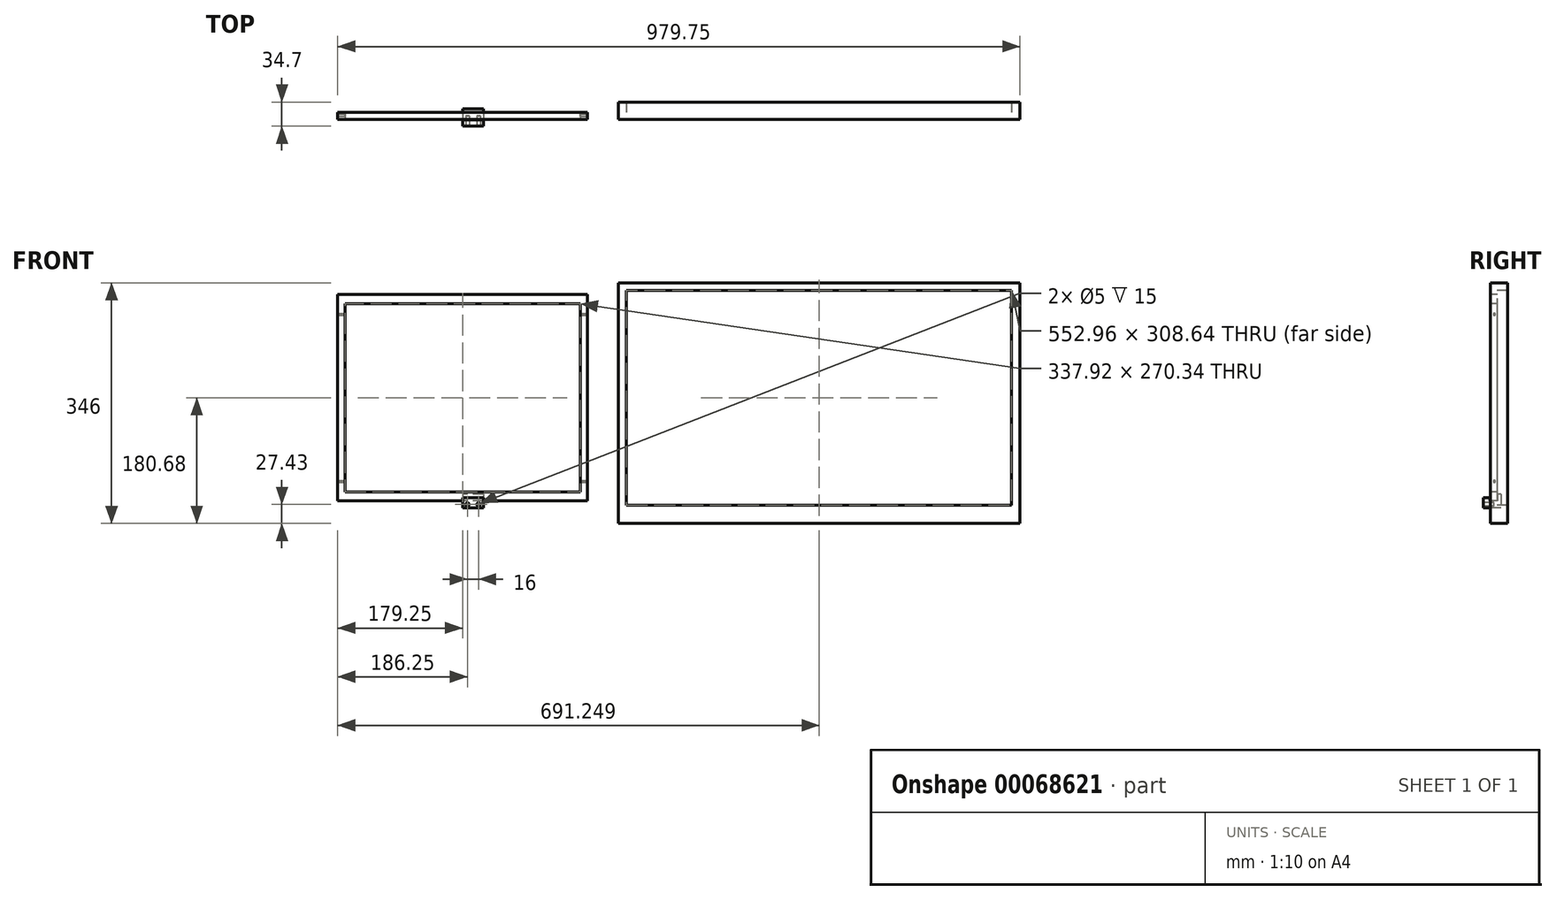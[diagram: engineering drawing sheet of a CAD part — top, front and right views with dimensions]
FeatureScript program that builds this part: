
annotation { "Feature Type Name" : "Feature", "Feature Type Description" : "" }
export const myFeature = defineFeature(function(context is Context, id is Id, definition is map)
    precondition{}
    {
        {
            var Q0;
            Q0=qCreatedBy(makeId("Front.planeOp"),FACE);
            var sketch = newSketch(context, id + "F0", { "sketchPlane" : qUnion([Q0])});
            skLineSegment(sketch, "E0.bottom", {"start": v(168.96, -135.17) * mm, "end": v(-168.96, -135.17) * mm});
            skLineSegment(sketch, "E0.top", {"start": v(168.96, 135.17) * mm, "end": v(-168.96, 135.17) * mm});
            skLineSegment(sketch, "E0.left", {"start": v(168.96, -135.17) * mm, "end": v(168.96, 135.17) * mm});
            skLineSegment(sketch, "E0.right", {"start": v(-168.96, -135.17) * mm, "end": v(-168.96, 135.17) * mm});
            skPoint(sketch, "E0.middle", {"position": v(0, 0) * mm});
            skLineSegment(sketch, "E1.bottom", {"start": v(179.25, -148.25) * mm, "end": v(-179.25, -148.25) * mm});
            skLineSegment(sketch, "E1.top", {"start": v(179.25, 148.25) * mm, "end": v(-179.25, 148.25) * mm});
            skLineSegment(sketch, "E1.left", {"start": v(179.25, -148.25) * mm, "end": v(179.25, 148.25) * mm});
            skLineSegment(sketch, "E1.right", {"start": v(-179.25, -148.25) * mm, "end": v(-179.25, 148.25) * mm});
            skSolve(sketch);
        }
        {
            var Q0;
            Q0 = qSketchRegion(id + "F0", true);
            extrude(context, id + "F1", {"entities" : qUnion([Q0]), "oppositeDirection" : true, "depth" : 10.3 * mm});
        }
        {
            var Q0;
            Q0=makeQuery(id+"F1.opExtrude","SWEPT_FACE",FACE,{"disambiguationData":[OSD([sQuery(id+"F0.wireOp",EDGE,"E1.left")])]});
            var sketch = newSketch(context, id + "F2", { "sketchPlane" : qUnion([Q0])});
            skCircle(sketch, "E2", {"center": v(6, 120) * mm, "radius": 1.5 * mm});
            skCircle(sketch, "E3", {"center": v(6, -120) * mm, "radius": 1.5 * mm});
            skSolve(sketch);
        }
        {
            var Q0;
            Q0 = qSketchRegion(id + "F2", true);
            extrude(context, id + "F3", {"entities" : qUnion([Q0]), "operationType" : NewBodyOperationType.REMOVE, "oppositeDirection" : true, "depth" : 390 * mm});
        }
        {
            var Q0;
            Q0=qCreatedBy(makeId("Right.planeOp"),FACE);
            var sketch = newSketch(context, id + "F4", { "sketchPlane" : qUnion([Q0])});
            skLineSegment(sketch, "E4.bottom", {"start": v(15.3, -158.25) * mm, "end": v(-9.7, -158.25) * mm});
            skLineSegment(sketch, "E4.left", {"start": v(15.3, -138.25) * mm, "end": v(15.3, -158.25) * mm});
            skLineSegment(sketch, "E4.right", {"start": v(-9.7, -143.25) * mm, "end": v(-9.7, -158.25) * mm});
            skLineSegment(sketch, "E5", {"start": v(15.3, -138.25) * mm, "end": v(10.3, -138.25) * mm});
            skLineSegment(sketch, "E6", {"start": v(10.3, -138.25) * mm, "end": v(10.3, -148.25) * mm});
            skLineSegment(sketch, "E7", {"start": v(10.3, -148.25) * mm, "end": v(-0.7, -148.25) * mm});
            skLineSegment(sketch, "E8", {"start": v(-0.7, -148.25) * mm, "end": v(-0.7, -143.25) * mm});
            skLineSegment(sketch, "E9", {"start": v(-0.7, -143.25) * mm, "end": v(-9.7, -143.25) * mm});
            skSolve(sketch);
        }
        {
            var Q0;
            Q0 = qSketchRegion(id + "F4", true);
            extrude(context, id + "F5", {"entities" : qUnion([Q0]), "depth" : 30 * mm});
        }
        {
            var Q0;
            Q0=makeQuery(id+"F5.opExtrude","SWEPT_FACE",FACE,{"disambiguationData":[OSD([sQuery(id+"F4.wireOp",EDGE,"E4.right")])]});
            var sketch = newSketch(context, id + "F6", { "sketchPlane" : qUnion([Q0])});
            skCircle(sketch, "E10", {"center": v(7, -153.25) * mm, "radius": 2.5 * mm});
            skCircle(sketch, "E11", {"center": v(23, -153.25) * mm, "radius": 2.5 * mm});
            skSolve(sketch);
        }
        {
            var Q0;
            Q0=makeQuery(id+"F6.imprint","IMPRINT",FACE,{"disambiguationData":[TD([[makeQuery(id+"F6.imprint","IMPRINT",EDGE,{"derivedFrom":sQuery(id+"F6.wireOp",EDGE,"E10")}),1.0]])]});
            var Q1;
            Q1=makeQuery(id+"F6.imprint","IMPRINT",FACE,{"disambiguationData":[TD([[makeQuery(id+"F6.imprint","IMPRINT",EDGE,{"derivedFrom":sQuery(id+"F6.wireOp",EDGE,"E11")}),1.0]])]});
            extrude(context, id + "F7", {"entities" : qUnion([Q0, Q1]), "operationType" : NewBodyOperationType.REMOVE, "oppositeDirection" : true, "depth" : 15 * mm});
        }
        {
            var Q0;
            Q0=qCreatedBy(makeId("Front.planeOp"),FACE);
            var sketch = newSketch(context, id + "F8", { "sketchPlane" : qUnion([Q0])});
            skLineSegment(sketch, "E12.bottom", {"start": v(788.48, -154.32) * mm, "end": v(235.52, -154.32) * mm});
            skLineSegment(sketch, "E12.top", {"start": v(788.48, 154.32) * mm, "end": v(235.52, 154.32) * mm});
            skLineSegment(sketch, "E12.left", {"start": v(788.48, -154.32) * mm, "end": v(788.48, 154.32) * mm});
            skLineSegment(sketch, "E12.right", {"start": v(235.52, -154.32) * mm, "end": v(235.52, 154.32) * mm});
            skPoint(sketch, "E12.middle", {"position": v(512, 0) * mm});
            skLineSegment(sketch, "E13.bottom", {"start": v(800.5, -180.68) * mm, "end": v(223.5, -180.68) * mm});
            skLineSegment(sketch, "E13.top", {"start": v(800.5, 165.32) * mm, "end": v(223.5, 165.32) * mm});
            skLineSegment(sketch, "E13.left", {"start": v(800.5, -180.68) * mm, "end": v(800.5, 165.32) * mm});
            skLineSegment(sketch, "E13.right", {"start": v(223.5, -180.68) * mm, "end": v(223.5, 165.32) * mm});
            skPoint(sketch, "E13.middle", {"position": v(512, -7.68) * mm});
            skSolve(sketch);
        }
        {
            var Q0;
            Q0=makeQuery(id+"F8.imprint","IMPRINT",FACE,{"disambiguationData":[TD([[makeQuery(id+"F8.imprint","IMPRINT",EDGE,{"derivedFrom":sQuery(id+"F8.wireOp",EDGE,"E12.bottom")}),1.0]])]});
            extrude(context, id + "F9", {"entities" : qUnion([Q0]), "oppositeDirection" : true, "depth" : 25 * mm});
        }
    });
